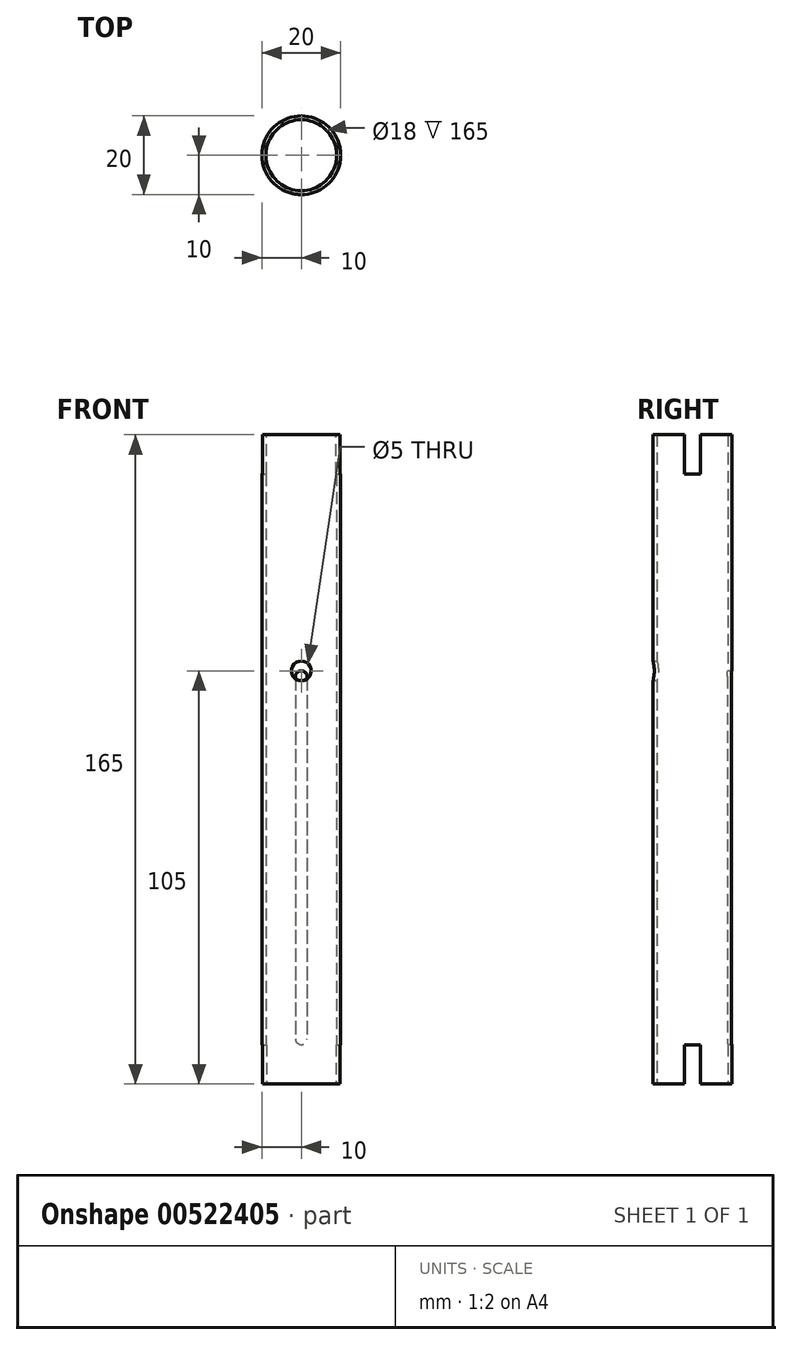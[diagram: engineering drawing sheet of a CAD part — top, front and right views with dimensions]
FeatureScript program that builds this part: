
annotation { "Feature Type Name" : "Feature", "Feature Type Description" : "" }
export const myFeature = defineFeature(function(context is Context, id is Id, definition is map)
    precondition{}
    {
        {
            var Q0;
            Q0=qCreatedBy(makeId("Top.planeOp"),FACE);
            var sketch = newSketch(context, id + "F0", { "sketchPlane" : qUnion([Q0])});
            skCircle(sketch, "E0", {"center": v(0, 0) * mm, "radius": 10 * mm});
            skCircle(sketch, "E1", {"center": v(0, 0) * mm, "radius": 9 * mm});
            skSolve(sketch);
        }
        {
            var Q0;
            Q0=makeQuery(id+"F0.imprint","IMPRINT",FACE,{"disambiguationData":[TD([[makeQuery(id+"F0.imprint","IMPRINT",EDGE,{"derivedFrom":sQuery(id+"F0.wireOp",EDGE,"E0")}),1.0]])]});
            extrude(context, id + "F1", {"entities" : qUnion([Q0]), "depth" : 165 * mm, "offsetDistance" : 25 * mm});
        }
        {
            var Q0;
            Q0=qCreatedBy(makeId("Top.planeOp"),FACE);
            var sketch = newSketch(context, id + "F2", { "sketchPlane" : qUnion([Q0])});
            skCircle(sketch, "E2", {"center": v(0, 0) * mm, "radius": 10 * mm});
            skLineSegment(sketch, "E3", {"start": v(-9.8, -2) * mm, "end": v(9.8, -2) * mm});
            skLineSegment(sketch, "E4", {"start": v(-9.8, 2) * mm, "end": v(9.8, 2) * mm});
            skSolve(sketch);
        }
        {
            var Q0;
            {var subQ0=sQuery(id+"F2.wireOp",EDGE,"E3");Q0=makeQuery(id+"F2.imprint","IMPRINT",FACE,{"disambiguationData":[TD([[makeQuery(id+"F2.imprint","IMPRINT",EDGE,{"derivedFrom":subQ0}),1.0]])]});}
            extrude(context, id + "F3", {"entities" : qUnion([Q0]), "operationType" : NewBodyOperationType.REMOVE, "depth" : 10 * mm, "offsetDistance" : 25 * mm});
        }
        {
            var Q0;
            Q0=qCreatedBy(makeId("Front.planeOp"),FACE);
            var sketch = newSketch(context, id + "F4", { "sketchPlane" : qUnion([Q0])});
            skCircle(sketch, "E5", {"center": v(0, 11.5) * mm, "radius": 1.5 * mm});
            skCircle(sketch, "E6", {"center": v(0, 103.5) * mm, "radius": 1.5 * mm});
            skLineSegment(sketch, "E7", {"start": v(1.5, 103.5) * mm, "end": v(1.5, 11.5) * mm});
            skLineSegment(sketch, "E8", {"start": v(-1.5, 11.5) * mm, "end": v(-1.5, 103.5) * mm});
            skSolve(sketch);
        }
        {
            var Q0;
            Q0 = qSketchRegion(id + "F4", true);
            extrude(context, id + "F5", {"entities" : qUnion([Q0]), "operationType" : NewBodyOperationType.REMOVE, "oppositeDirection" : true, "depth" : 25 * mm, "offsetDistance" : 25 * mm});
        }
        {
            var Q0;
            Q0=makeQuery(id+"F1.opExtrude","CAP_FACE",FACE,{"disambiguationData":[OSD([sQuery(id+"F0.wireOp",EDGE,"E0"),sQuery(id+"F0.wireOp",EDGE,"E1")])],"isStart":false});
            var sketch = newSketch(context, id + "F6", { "sketchPlane" : qUnion([Q0])});
            skLineSegment(sketch, "E9", {"start": v(-9.8, 2) * mm, "end": v(9.8, 2) * mm});
            skLineSegment(sketch, "E10", {"start": v(-9.8, -2) * mm, "end": v(9.8, -2) * mm});
            skSolve(sketch);
        }
        {
            var Q0;
            {var subQ0=sQuery(id+"F6.wireOp",EDGE,"E9");var subQ1=makeQuery(id+"F1.opExtrude","CAP_EDGE",EDGE,{"disambiguationData":[OSD([sQuery(id+"F0.wireOp",EDGE,"E0")])],"isStart":false});var subQ2=makeQuery(id+"F6.imprint","INTERSECT",VERTEX,{"disambiguationData":[OD(0.0)],"derivedFrom":[subQ1,subQ0]});Q0=makeQuery(id+"F6.imprint","IMPRINT",FACE,{"disambiguationData":[TD([[makeQuery(id+"F6.imprint","IMPRINT",EDGE,{"disambiguationData":[TD([[subQ2,-1.0]])],"derivedFrom":subQ0}),-1.0]])]});}
            var Q1;
            {var subQ0=sQuery(id+"F6.wireOp",EDGE,"E9");var subQ1=makeQuery(id+"F1.opExtrude","CAP_EDGE",EDGE,{"disambiguationData":[OSD([sQuery(id+"F0.wireOp",EDGE,"E0")])],"isStart":false});var subQ2=makeQuery(id+"F6.imprint","INTERSECT",VERTEX,{"disambiguationData":[OD(1.0)],"derivedFrom":[subQ1,subQ0]});Q1=makeQuery(id+"F6.imprint","IMPRINT",FACE,{"disambiguationData":[TD([[makeQuery(id+"F6.imprint","IMPRINT",EDGE,{"disambiguationData":[TD([[subQ2,1.0]])],"derivedFrom":subQ0}),-1.0]])]});}
            extrude(context, id + "F7", {"entities" : qUnion([Q0, Q1]), "operationType" : NewBodyOperationType.REMOVE, "oppositeDirection" : true, "depth" : 10 * mm, "offsetDistance" : 25 * mm});
        }
        {
            var Q0;
            Q0=qCreatedBy(makeId("Front.planeOp"),FACE);
            var sketch = newSketch(context, id + "F8", { "sketchPlane" : qUnion([Q0])});
            skCircle(sketch, "E11", {"center": v(0, 105) * mm, "radius": 2.5 * mm});
            skSolve(sketch);
        }
        {
            var Q0;
            Q0 = qSketchRegion(id + "F8", true);
            extrude(context, id + "F9", {"entities" : qUnion([Q0]), "operationType" : NewBodyOperationType.REMOVE, "depth" : 25 * mm, "offsetDistance" : 25 * mm});
        }
    });
